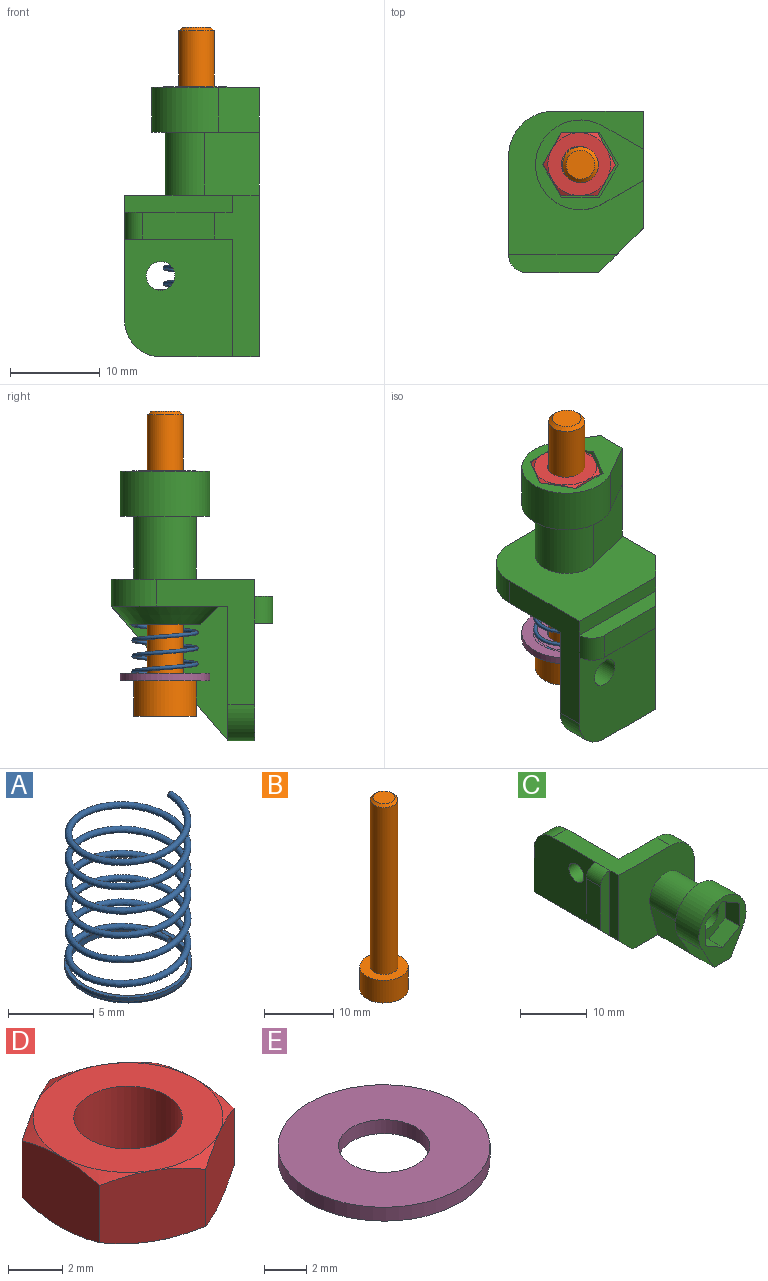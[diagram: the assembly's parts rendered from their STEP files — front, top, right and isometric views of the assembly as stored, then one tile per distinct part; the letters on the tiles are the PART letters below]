
ASSEMBLY  parts=5 mates=4
PART A: 8 faces, bbox 8.2x8.2x11.1 mm
  f0: bspline ~10.9x7.4mm, area 163.9mm2, adj f1,f2,f3,f4,f6
  f1: plane 0.46x0.26mm, normal (0,-1,0), area 0.1mm2, adj f0,f3
  f2: plane 0.46x0.46mm, normal (0,1,0), area 0.1mm2, adj f0
  f3: cylinder r=3.5mm len=7mm, axis (0,0,-1), area 9.7mm2, adj f0,f1,f4,f6,f7
  f4: cylinder r=3.5mm len=0.66mm, axis (0,0,-1), area 0mm2, adj f0,f3,f6
  f5: cylinder r=3.75mm len=7.5mm, axis (0,0,-1), area 5.9mm2, adj f6,f7
  f6: plane 7.61x7.61mm, normal (0,0,1), area 4.9mm2, adj f0,f3,f4,f5
  f7: torus R=3.5mm, axis (0,0,1), area 9mm2, adj f3,f5
PART B: 13 faces, bbox 7x7x34 mm
  f0: plane 7x7mm, normal (0,0,-1), area 30.7mm2, adj f2,f6,f7,f8,f9,f10,f11
  f1: plane 3.2x3.2mm, normal (0,0,1), area 8mm2, adj f5
  f2: cylinder r=3.5mm len=7mm, axis (0,0,-1), area 88mm2, adj f0,f3
  f3: plane 7x7mm, normal (0,0,1), area 25.9mm2, adj f2,f4
  f4: cylinder r=2mm len=29.6mm, axis (0,0,-1), area 372mm2, adj f3,f5
  f5: cone r=2mm half-angle=45deg, axis (0,0,-1), area 6.4mm2, adj f1,f4
  f6: plane 2x1.73mm, normal (-1,0,0), area 3.5mm2, adj f0,f7,f11,f12
  f7: plane 2x1.5mm, normal (-0.5,-0.87,0), area 3.5mm2, adj f0,f6,f8,f12
  f8: plane 2x1.5mm, normal (0.5,-0.87,0), area 3.5mm2, adj f0,f7,f9,f12
  f9: plane 2x1.73mm, normal (1,0,0), area 3.5mm2, adj f0,f8,f10,f12
  f10: plane 2x1.5mm, normal (0.5,0.87,0), area 3.5mm2, adj f0,f9,f11,f12
  f11: plane 2x1.5mm, normal (-0.5,0.87,0), area 3.5mm2, adj f0,f6,f10,f12
  f12: plane 3.46x3mm, normal (0,0,-1), area 7.8mm2, adj f6,f7,f8,f9,f10,f11
PART C: 39 faces, bbox 18x30x15 mm
  f0: plane 16x15mm, normal (0,-1,0), area 173.5mm2, adj f5,f6,f9,f11,f17,f33,f36,f37
  f1: plane 13x13mm, normal (0,1,0), area 47.1mm2, adj f2,f6,f7,f9,f17,f26,f27
  f2: plane 15x13mm, normal (0,0,1), area 77.5mm2, adj f1,f7,f10,f24,f25,f27
  f3: cylinder r=2.15mm len=14mm, axis (0,1,0), area 189.1mm2, adj f24,f34
  f4: plane 13.1x12mm, normal (-1,0,0), area 145.7mm2, adj f8,f9,f12,f14,f32,f33
  f5: plane 12x1.9mm, normal (-1,0,0), area 22.8mm2, adj f0,f9,f13,f33
  f6: plane 10x3mm, normal (1,0,0), area 30mm2, adj f0,f1,f10,f11,f17,f25
  f7: plane 15x13mm, normal (1,0,0), area 183.5mm2, adj f1,f2,f8,f9,f12,f32
  f8: plane 11x3mm, normal (0,1,0), area 28.5mm2, adj f4,f7,f10,f32,f33
  f9: plane 14x11mm, normal (0,0,1), area 66mm2, adj f0,f1,f4,f5,f7,f16,f17,f32
  f10: plane 15x13mm, normal (0.76,0.65,0), area 39.7mm2, adj f2,f6,f8,f11
  f11: plane 30x13mm, normal (0,0,-1), area 178.1mm2, adj f0,f6,f10,f28,f30,f31,f33,f37
  f12: cylinder r=1.6mm len=3.2mm, axis (1,0,0), area 30.2mm2, adj f4,f7
  f13: plane 12x2mm, normal (0,-1,0), area 21.1mm2, adj f5,f15,f16,f33
  f14: plane 12x2mm, normal (0,1,0), area 21.1mm2, adj f4,f15,f16,f33
  f15: plane 8x3mm, normal (-1,0,0), area 24mm2, adj f13,f14,f16,f33
  f16: cylinder r=2mm len=3mm, axis (0,1,0), area 9.4mm2, adj f9,f13,f14,f15
  f17: cylinder r=5mm len=5mm, axis (0,-1,0), area 23.6mm2, adj f0,f1,f6,f9
  f18: plane 3.65x3mm, normal (-0.5,0,-0.87), area 12.6mm2, adj f19,f23,f28,f34
  f19: plane 4.21x3mm, normal (-1,0,0), area 12.6mm2, adj f18,f20,f28,f34
  f20: plane 3.65x3mm, normal (-0.5,0,0.87), area 12.6mm2, adj f19,f21,f28,f34
  f21: plane 3.65x3mm, normal (0.5,0,0.87), area 12.6mm2, adj f20,f22,f28,f34
  f22: plane 4.21x3mm, normal (1,0,0), area 12.6mm2, adj f21,f23,f28,f34
  f23: plane 3.65x3mm, normal (0.5,0,-0.87), area 12.6mm2, adj f18,f22,f28,f34
  f24: plane 9x8mm, normal (0,1,0), area 50.6mm2, adj f2,f3,f25,f26,f27
  f25: plane 5x2mm, normal (0.71,0.71,0), area 14.1mm2, adj f2,f6,f24,f26
  f26: cone r=4mm half-angle=45deg, axis (0,-1,0), area 44.4mm2, adj f1,f24,f25,f27
  f27: plane 5x2mm, normal (-0.71,0.71,0), area 14.1mm2, adj f1,f2,f24,f26
  f28: plane 12x10mm, normal (0,-1,0), area 44.3mm2, adj f11,f18,f19,f20,f21,f22,f23,f29
  f29: cylinder r=5mm len=10mm, axis (0,1,0), area 104.7mm2, adj f28,f30,f31,f35
  f30: plane 5x4.5mm, normal (-0.87,0,-0.5), area 26mm2, adj f11,f28,f29,f35
  f31: plane 5x4.5mm, normal (0.87,0,-0.5), area 26mm2, adj f11,f28,f29,f35
  f32: cylinder r=4mm len=4mm, axis (1,0,0), area 18.8mm2, adj f4,f7,f8,f9
  f33: plane 18x5mm, normal (-0.71,0,-0.71), area 84.9mm2, adj f0,f4,f5,f8,f11,f13,f14,f15
  f34: plane 8.43x7.3mm, normal (0,-1,0), area 31.6mm2, adj f3,f18,f19,f20,f21,f22,f23
  f35: plane 12x10mm, normal (0,1,0), area 33.8mm2, adj f29,f30,f31,f36,f37,f38
  f36: cylinder r=3.5mm len=7mm, axis (0,1,0), area 89.9mm2, adj f0,f35,f37,f38
  f37: plane 7x6.09mm, normal (-0.97,0,-0.26), area 44.1mm2, adj f0,f11,f35,f36
  f38: plane 7x6.09mm, normal (0.97,0,-0.26), area 44.1mm2, adj f0,f11,f35,f36
PART D: 21 faces, bbox 8.4x8.4x3.5 mm
  f0: plane 7x7mm, normal (0,0,1), area 25.9mm2, adj f2,f3,f4,f7,f9,f11,f13
  f1: plane 7x7mm, normal (0,0,-1), area 25.9mm2, adj f2,f5,f6,f8,f10,f12,f14
  f2: cylinder r=2mm len=4mm, axis (0,0,-1), area 40.2mm2, adj f0,f1
  f3: cone r=4.04mm half-angle=60deg, axis (0,0,-1), area 1.2mm2, adj f0,f15,f20
  f4: cone r=4.04mm half-angle=60deg, axis (0,0,-1), area 1.2mm2, adj f0,f15,f16
  f5: cone r=4.04mm half-angle=60deg, axis (0,0,1), area 1.2mm2, adj f1,f15,f20
  f6: cone r=4.04mm half-angle=60deg, axis (0,0,1), area 1.2mm2, adj f1,f15,f16
  f7: cone r=4.04mm half-angle=60deg, axis (0,0,-1), area 1.2mm2, adj f0,f16,f17
  f8: cone r=4.04mm half-angle=60deg, axis (0,0,1), area 1.2mm2, adj f1,f16,f17
  f9: cone r=4.04mm half-angle=60deg, axis (0,0,-1), area 1.2mm2, adj f0,f17,f18
  f10: cone r=4.04mm half-angle=60deg, axis (0,0,1), area 1.2mm2, adj f1,f17,f18
  f11: cone r=4.04mm half-angle=60deg, axis (0,0,-1), area 1.2mm2, adj f0,f18,f19
  f12: cone r=4.04mm half-angle=60deg, axis (0,0,1), area 1.2mm2, adj f1,f18,f19
  f13: cone r=4.04mm half-angle=60deg, axis (0,0,-1), area 1.2mm2, adj f0,f19,f20
  f14: cone r=4.04mm half-angle=60deg, axis (0,0,1), area 1.2mm2, adj f1,f19,f20
  f15: plane 3.83x3.54mm, normal (0.5,-0.87,0), area 12.1mm2, adj f3,f4,f5,f6,f16,f20
  f16: plane 3.83x3.54mm, normal (-0.5,-0.87,0), area 12.1mm2, adj f4,f6,f7,f8,f15,f17
  f17: plane 4.38x3.53mm, normal (-1,0,0), area 12.1mm2, adj f7,f8,f9,f10,f16,f18
  f18: plane 3.83x3.54mm, normal (-0.5,0.87,0), area 12.1mm2, adj f9,f10,f11,f12,f17,f19
  f19: plane 3.83x3.54mm, normal (0.5,0.87,0), area 12.1mm2, adj f11,f12,f13,f14,f18,f20
  f20: plane 4.38x3.53mm, normal (1,0,0), area 12.1mm2, adj f3,f5,f13,f14,f15,f19
PART E: 4 faces, bbox 10x10x0.8 mm
  f0: cylinder r=5mm len=10mm, axis (0,0,-1), area 25.1mm2, adj f1,f2
  f1: plane 10x10mm, normal (0,0,1), area 64mm2, adj f0,f3
  f2: plane 10x10mm, normal (0,0,-1), area 64mm2, adj f0,f3
  f3: cylinder r=2.15mm len=4.3mm, axis (0,0,-1), area 10.8mm2, adj f1,f2
PLACE A t=(-2.32,3.7,-14.33)mm
PLACE B t=(-82.52,-6.1,-18.88)mm
PLACE C rot(axis=(-0.58,-0.58,0.58),120deg) t=(2.68,-6.3,-3.58)mm fixed
PLACE D rot(axis=(0,0,-1),30deg) t=(-16.11,0.12,5.32)mm
PLACE E rot(axis=(-1,0,0),180deg) t=(-42.32,23.7,-14.08)mm
MATE slider B.f2 <-> C.f26  axis (0,0,-1) through (-2.32,3.7,-0.08)mm
MATE fastened A.f3 <-> E.f0  axis (0,0,1) through (-2.32,3.7,-14.08)mm
MATE fastened D.f17 <-> C.f18  axis (-0.87,0.5,0) through (-5.48,5.53,6.92)mm
MATE fastened E.f0 <-> B.f2  axis (0,0,-1) through (-2.32,3.7,-14.88)mm
